# Revit family: Colector_RKM2001-SO31061
name_source: partatom
category: Aparatos eléctricos
revit_build: Autodesk Revit 2016 (Build: 20150220_1215(x64)
units: mm (PartAtom-declared; Revit-internal decimal feet)

## family parameters
Compartido = No
Corte con vacíos al cargar = No
Cota de conector redondo = Diámetro de uso
Mantener orientación de anotación = No
Número OmniClass = 23.80.00.00
Punto de cálculo de habitación = No
Se basa en plano de trabajo = No
Siempre vertical = Sí
Tipo de pieza = Caja de conexiones
Título OmniClass = Electric Power and Lighting

## types (1)
- RKM2001
    Altura = 73 mm
    Anchura = 1170 mm
    Carcasa captador = Marco aluminio
    Carga viento/nieve = 120km/h - 250 kg
    Contraseña homologación = GPS 8543
    Costo = 0 $
    Cristal = 3,2 mm vidrio seguridad solar templado ESG
    Código de montaje = SO31061
    Descripción = COLECTOR SOLAR RK
    Fabricante = SALVADOR ESCODA
    Imagen de tipo = alpin_RKM.jpg
    Longitud = 1730 mm
    Material absorbedor = Aluminio
    Modelo = RKM2001
    Peso = 28 kg
    Rendimiento térmico no / a1 / a2 = 0,755 - 3,745 W/m2K - 0,015 "/m2K2
    Revestimiento absorbedor = Altamente selectivo
    Superfície bruta = 2,02 m2
    URL = www.salvadorescoda.com
    Volúmen = 1,6 l
    Ángulo inclinación máx./mín. = 15º / 75º
